AUTODESK INVENTOR PART (.ipt)
format: ipt  version: 2022 (Build 260153000, 153)  size: 473,600 bytes
history: native  units: in
note: dims shown in document units (in); Inventor stores cm internally (conversion verified against a paired STEP export)
features: extrude x7, sketch x7, projected_geometry x4, fillet x2, plane x1, mirror x1, chamfer x1, pattern_linear x1
ambient origin geometry x8: Origin, YZ Plane, XZ Plane, XY Plane, X Axis, Y Axis, Z Axis, Center Point
bodies: Solid1 (feature_tree)
feature tree (24):
  extrude  "Extrusion1"  Depth=0.005in
  extrude  "Extrusion2"  Depth=0.125in TaperAngle=0.0deg
  plane  "Work Plane1"
  extrude  "Extrusion3"  Depth=0.0625in TaperAngle=0.0deg
  mirror  "Mirror1"
  extrude  "Extrusion4"  Depth=0.5in TaperAngle=0.0deg
  extrude  "Extrusion7"  Depth=1.9in
  extrude  "Extrusion8"  Depth=1.0in TaperAngle=0.0deg
  chamfer  "Chamfer2"  Distance=5.0in
  fillet  "Fillet1"  Radius=0.25in
  extrude  "Extrusion9"  Depth=0.125in
  pattern_linear  "Rectangular Pattern1"  Spacing1=0.1in  [1 undecoded]
  fillet  "Fillet2"  Radius=0.06in
  sketch  "Sketch1"  dims[d0=1.0in d1=0.0in d2=0.005in]
  sketch  "Sketch3"  dims[d3=1.5in d4=0.125in d5=0.0in]
  sketch  "Sketch4"  dims[d6=0.5in d7=0.0625in d8=0.0in]
  projected_geometry  "Projected Loop1"
  sketch  "Sketch5"  dims[d9=0.0625in d10=0.5in d11=0.0in]
  sketch  "Sketch8"  dims[d24=0.75in d25=1.9in]
  projected_geometry  "Projected Loop2"
  sketch  "Sketch9"  dims[d26=0.06in d27=1.0in d28=0.0in]
  projected_geometry  "Projected Loop3"
  sketch  "Sketch10"  dims[d29=1.0in d30=5.0in d31=0.0in d32=0.25in d33=0.125in d34=45.0deg d35=0.125in d36=0.1in d37=0.06in d38=0.0in d39=1.5748in d41=0.5in d42=0.06in]
  projected_geometry  "Projected Loop4"
note: 1 required parameter value undecoded (feature->parameter linkage not recoverable at this tier; creation-order binding heuristic only, values carry confidence <= 0.55)
